AUTODESK INVENTOR PART (.ipt)
format: ipt  version: 2017 (Build 210142000, 142)  size: 119,808 bytes
history: native  units: mm
features: other x1, extrude x1, sketch x1
ambient origin geometry x8: Origin, YZ Plane, XZ Plane, XY Plane, X Axis, Y Axis, Z Axis, Center Point
bodies: Body1 (feature_tree)
feature tree (3):
  other  "Sólido1"
  extrude  "Extrusión1"  Depth=120.0mm
  sketch  "Boceto1"  dims[d0=2.0mm d1=120.0mm d2=40.0mm d3=4.0mm d4=40.0mm d5=30.0mm d6=8.0mm d7=4.0mm d8=20.0mm d9=4.0mm d10=0.0mm]
